# Revit family: Hager-Orion_Inox-IP66-D210-Cl.I-Inox_encl-630A-500mm-CH-de
name_source: partatom
category: Electrical Equipment
units: mm (PartAtom-declared; Revit-internal decimal feet)

## family parameters
Cut with Voids When Loaded = No
Host = Face
Panel Configuration = Two Columns, Circuits Across
Part Type = Panelboard
Room Calculation Point = No
Round Connector Dimension = Use Diameter
Shared = No

## types (8) — shared parameters
EF000003 - Montageart = EV000384 - Aufputz
EF000007 - Farbe = EV000154 - sonstige
EF000040 - Höhe = 500 mm  [stored 1.64042 ft]
EF000049 - Tiefe = 210 mm  [stored 0.688976 ft]
EF000118 - Mit Montageplatte = No
EF000339 - Art der Abdeckung = EV004216 - Tür
EF001088 - Anbaumöglichkeit = Yes
EF001131 - Innentiefe = 176 mm
EF001596 - Werkstoff des Gehäuses = EV000166 - rostfreier Stahl
EF003532 - Geeignet für Außengebrauch = Yes
EF004464 - Art der Tür = EV002646 - Einzel
EF005474 - Schutzart (IP) = EV006422 - IP66
EF007800 - Geeignet für Blitzschutz = No
EF008873 - Nennstrom (In) = 630 A
EF009170 - Materialstärke Gehäuse = 2 mm  [stored 0.00656168 ft]
EF009171 - Materialstärke Tür/Deckel = 2 mm  [stored 0.00656168 ft]
EF015940 - Deckel mit Überdruckentlastung = No
HG000002 - Mit tür = Yes
HG000003 - Bereich = Orion Inox
HG000006 - Unterputz = No
HG000009 - Doppelflügeligen Tür = No
HG000010 - Asymmetrische Türen = No
HG000023 - Gehäuse mit doppeltem Querschnitt = No
HG000024 - Höhe des unteren Teils = 800 mm  [stored 2.62467 ft]
HG000026 - Stehend auf dem Boden = No
Manufacturer = Hager
Type Comments = Orion Inox
zero-valued in all types: Default Elevation, EF000218 - Einbautiefe, EF000266 - Anzahl der Reihen, EF000437 - Anzahl der Leitungseinführungen, EF002950 - Breite in Teilungseinheiten, EF004427 - Anzahl der Module, EF009554 - Anzahl der Öffnungen für Flanschplatten, HG000027 - Sockelhöhe

## per-type parameters (varying)
| type | EF000008 - Breite | EF001613 - Funktionserhalt | EF004293 - Schlagfestigkeit | EF006244 - Transparenter Deckel/Tür | EF006306 - Mit Schloss | EF009212 - Ausführung Deckel | HG000004 - Herstellerreferenz |
| Aufputz IP66 B400 H500 T210  - FL021BW | 400 mm  [stored 1.31234 ft] |  | EV008784 - IK10 | No | No | EV009916 - mit Ausschnitt | FL021BW |
| Aufputz IP66 B400 H500 T210  - FL021BWL | 400 mm  [stored 1.31234 ft] |  | EV008784 - IK10 | No | No | EV009916 - mit Ausschnitt | FL021BWL |
| Aufputz IP66 B400 H500 T210  - FL021TW | 400 mm  [stored 1.31234 ft] | EV000494 - ohne | EV006814 - IK08 | Yes | Yes | EV000116 - geschlossen | FL021TW |
| Aufputz IP66 B400 H500 T210  - FL021TWL | 400 mm  [stored 1.31234 ft] | EV000494 - ohne | EV006814 - IK08 | Yes | Yes | EV000116 - geschlossen | FL021TWL |
| Aufputz IP66 B500 H500 T210  - FL023BW | 500 mm  [stored 1.64042 ft] | EV000494 - ohne | EV008784 - IK10 | No | Yes | EV000116 - geschlossen | FL023BW |
| Aufputz IP66 B500 H500 T210  - FL023BWL | 500 mm  [stored 1.64042 ft] | EV000494 - ohne | EV008784 - IK10 | No | Yes | EV000116 - geschlossen | FL023BWL |
| Aufputz IP66 B500 H500 T210  - FL023TW | 500 mm  [stored 1.64042 ft] | EV000494 - ohne | EV006814 - IK08 | Yes | Yes | EV000116 - geschlossen | FL023TW |
| Aufputz IP66 B500 H500 T210  - FL023TWL | 500 mm  [stored 1.64042 ft] | EV000494 - ohne | EV006814 - IK08 | Yes | Yes | EV000116 - geschlossen | FL023TWL |

note: [stored X ft] marks values corroborated as IEEE doubles in the binary element streams (Revit-internal decimal feet)

## geometry (parser evidence)
native form markers: Sweep x8
no freeform markers — native parametric forms only
